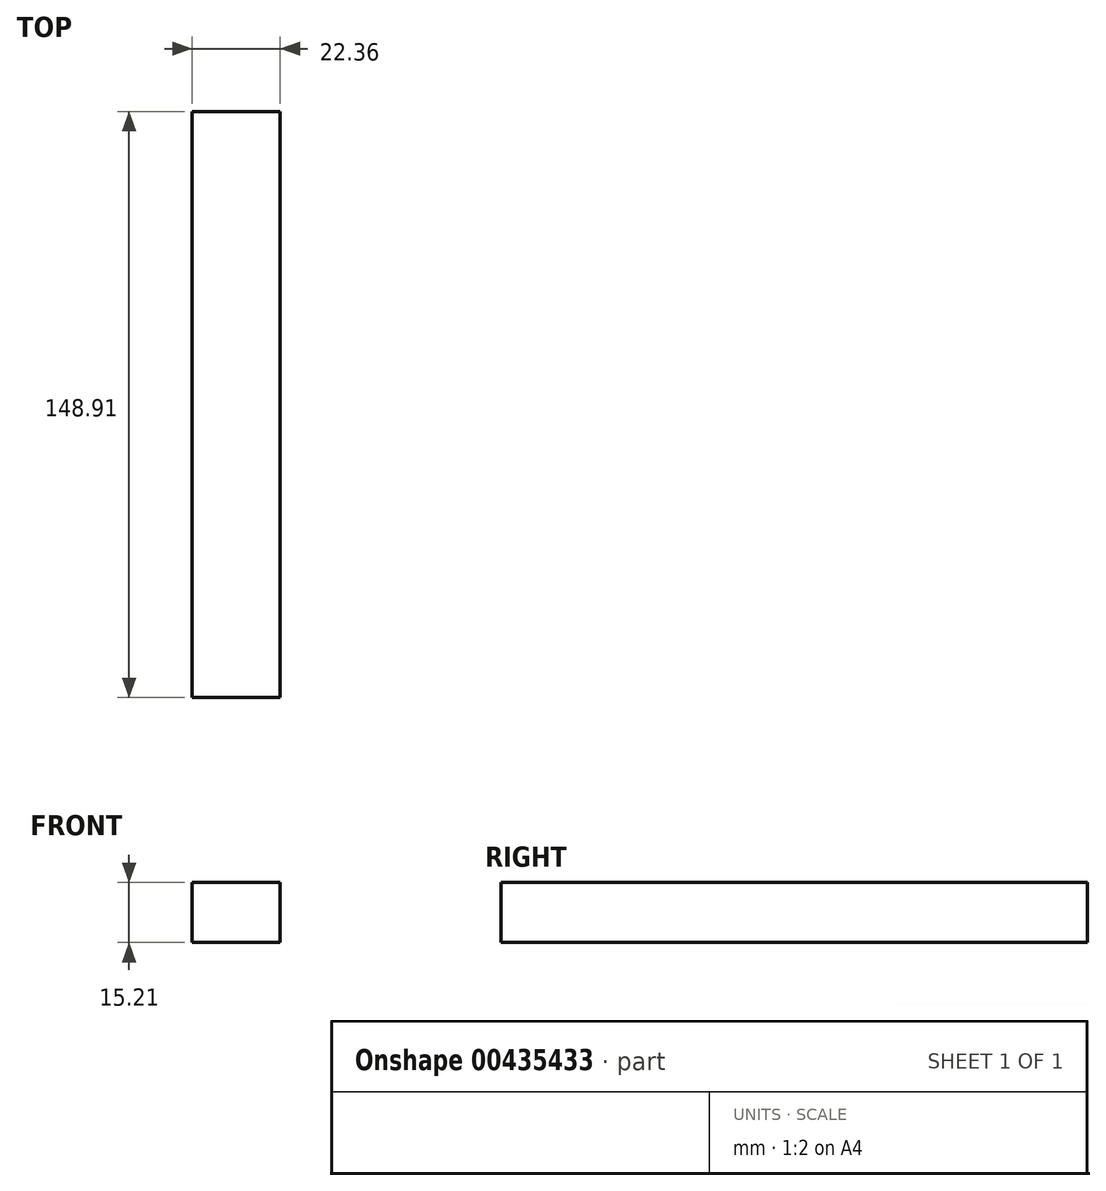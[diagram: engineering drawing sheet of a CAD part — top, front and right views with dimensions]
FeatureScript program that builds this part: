
annotation { "Feature Type Name" : "Feature", "Feature Type Description" : "" }
export const myFeature = defineFeature(function(context is Context, id is Id, definition is map)
    precondition{}
    {
        {
            var Q0;
            Q0=qCreatedBy(makeId("Front.planeOp"),FACE);
            var sketch = newSketch(context, id + "F0", { "sketchPlane" : qUnion([Q0])});
            skLineSegment(sketch, "E0.bottom", {"start": v(0, 0) * mm, "end": v(22.36, 0) * mm});
            skLineSegment(sketch, "E0.top", {"start": v(0, 15.21) * mm, "end": v(22.36, 15.21) * mm});
            skLineSegment(sketch, "E0.left", {"start": v(0, 0) * mm, "end": v(0, 15.21) * mm});
            skLineSegment(sketch, "E0.right", {"start": v(22.36, 0) * mm, "end": v(22.36, 15.21) * mm});
            skLineSegment(sketch, "E1.bottom", {"start": v(69.5, 82.82) * mm, "end": v(-73.5, 82.82) * mm, "construction": true});
            skLineSegment(sketch, "E1.top", {"start": v(69.5, -58.15) * mm, "end": v(-73.5, -58.15) * mm, "construction": true});
            skLineSegment(sketch, "E1.left", {"start": v(69.5, 82.82) * mm, "end": v(69.5, -58.15) * mm, "construction": true});
            skLineSegment(sketch, "E1.right", {"start": v(-73.5, 82.82) * mm, "end": v(-73.5, -58.15) * mm, "construction": true});
            skSolve(sketch);
        }
        {
            var Q0;
            Q0 = qBodyType(qCreatedBy(id + "F0" ,EDGE), BodyType.WIRE);
            var sketch = newSketch(context, id + "F1", { "sketchPlane" : qUnion([Q0])});
            skSolve(sketch);
        }
        {
            var Q0;
            Q0 = qSketchRegion(id + "F1", true);
            var Q1;
            Q1=makeQuery(id+"F0.imprint","IMPRINT",FACE,{"disambiguationData":[TD([[makeQuery(id+"F0.imprint","IMPRINT",EDGE,{"derivedFrom":sQuery(id+"F0.wireOp",EDGE,"E0.bottom")}),1.0]])]});
            extrude(context, id + "F2", {"entities" : qUnion([Q0, Q1]), "depth" : 148.9 * mm});
        }
    });
